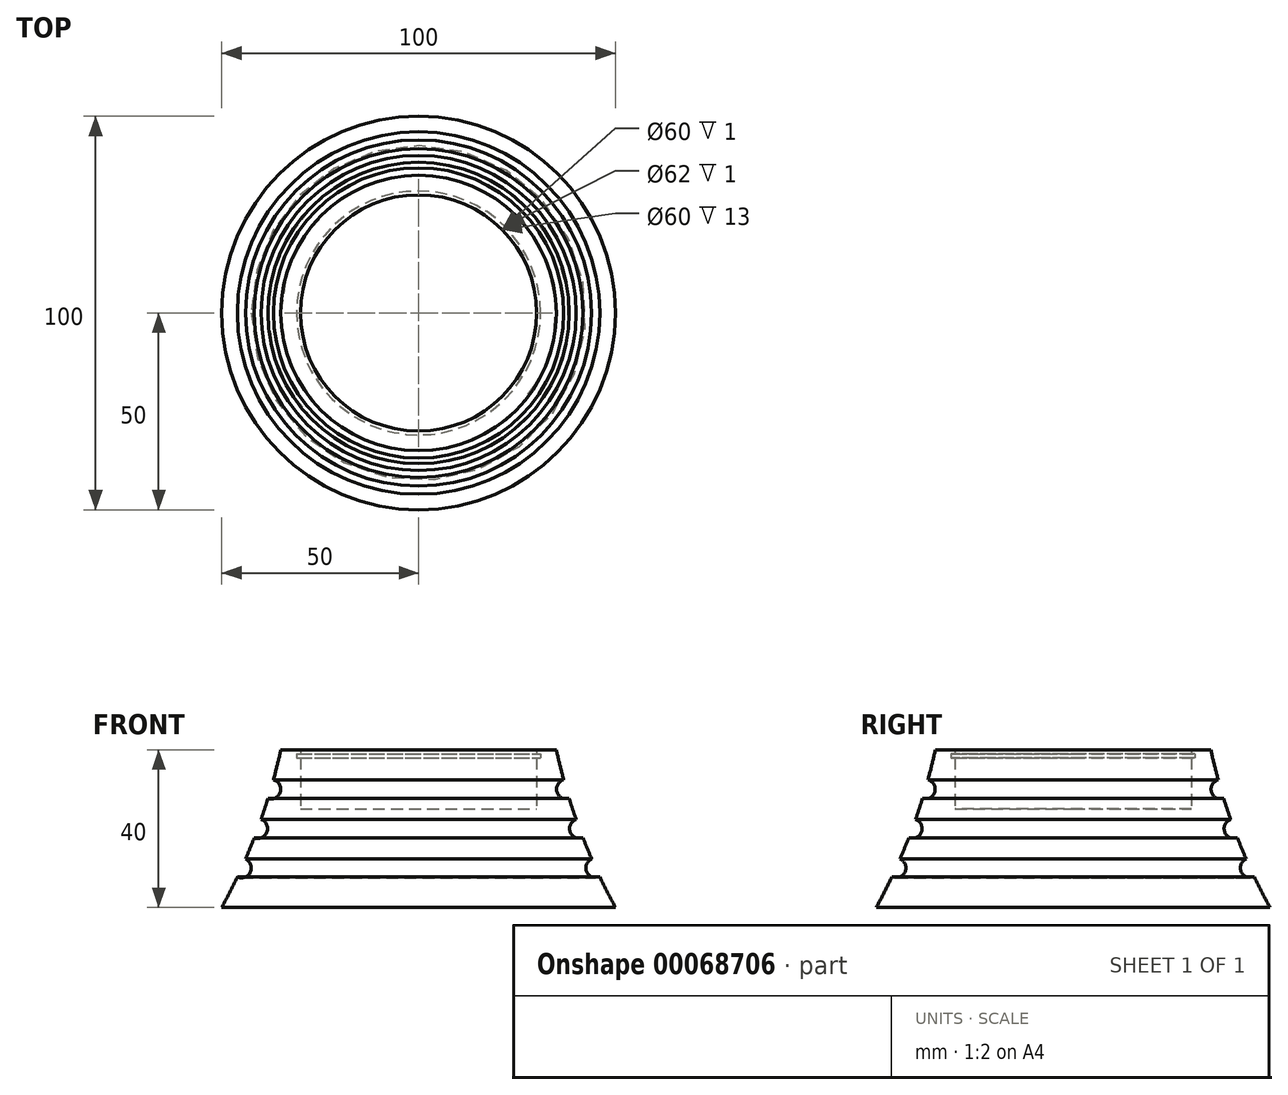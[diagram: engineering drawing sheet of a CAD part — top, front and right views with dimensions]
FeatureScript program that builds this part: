
annotation { "Feature Type Name" : "Feature", "Feature Type Description" : "" }
export const myFeature = defineFeature(function(context is Context, id is Id, definition is map)
    precondition{}
    {
        {
            var Q0;
            Q0=qCreatedBy(makeId("Front.planeOp"),FACE);
            var sketch = newSketch(context, id + "F0", { "sketchPlane" : qUnion([Q0])});
            skLineSegment(sketch, "E0", {"start": v(0, 0) * mm, "end": v(0, 25) * mm});
            skLineSegment(sketch, "E1", {"start": v(0, 25) * mm, "end": v(30, 25) * mm});
            skLineSegment(sketch, "E2", {"start": v(30, 25) * mm, "end": v(30, 38) * mm});
            skLineSegment(sketch, "E3", {"start": v(30, 40) * mm, "end": v(35, 40) * mm});
            skLineSegment(sketch, "E4", {"start": v(0, 0) * mm, "end": v(50, 0) * mm});
            skArc(sketch, "E5", {"start": v(35, 40) * mm, "mid": v(35.89, 36.2) * mm, "end": v(36.87, 32.4) * mm});
            skLineSegment(sketch, "E6", {"start": v(30, 39) * mm, "end": v(31, 39) * mm});
            skLineSegment(sketch, "E7", {"start": v(31, 39) * mm, "end": v(31, 38) * mm});
            skLineSegment(sketch, "E8", {"start": v(31, 38) * mm, "end": v(30, 38) * mm});
            skArc(sketch, "E9", {"start": v(36.87, 32.4) * mm, "mid": v(35.16, 29.3) * mm, "end": v(38.28, 27.6) * mm});
            skArc(sketch, "E10", {"start": v(40.02, 22.35) * mm, "mid": v(38.52, 19.13) * mm, "end": v(41.76, 17.66) * mm});
            skArc(sketch, "E11", {"start": v(43.97, 12.28) * mm, "mid": v(42.72, 8.96) * mm, "end": v(46.05, 7.73) * mm});
            skArc(sketch, "E12.trimOffspring", {"start": v(38.28, 27.6) * mm, "mid": v(39.12, 24.97) * mm, "end": v(40.02, 22.35) * mm});
            skArc(sketch, "E13.trimOffspring", {"start": v(41.76, 17.66) * mm, "mid": v(43.32, 13.8) * mm, "end": v(45, 10) * mm});
            skArc(sketch, "E14.trimOffspring", {"start": v(46.05, 7.73) * mm, "mid": v(47.97, 3.84) * mm, "end": v(50, 0) * mm});
            skLineSegment(sketch, "E15.trimOffspring", {"start": v(30, 39) * mm, "end": v(30, 40) * mm});
            skSolve(sketch);
        }
        {
            var Q0;
            Q0=makeQuery(id+"F0.imprint","IMPRINT",FACE,{"disambiguationData":[TD([[makeQuery(id+"F0.imprint","IMPRINT",EDGE,{"derivedFrom":sQuery(id+"F0.wireOp",EDGE,"E0")}),-1.0]])]});
            var Q1;
            Q1=sQuery(id+"F0.wireOp",EDGE,"E0");
            revolve(context, id + "F1", {"entities" : qUnion([Q0]), "axis" : qUnion([Q1]), "revolveType" : RevolveType.FULL});
        }
    });
